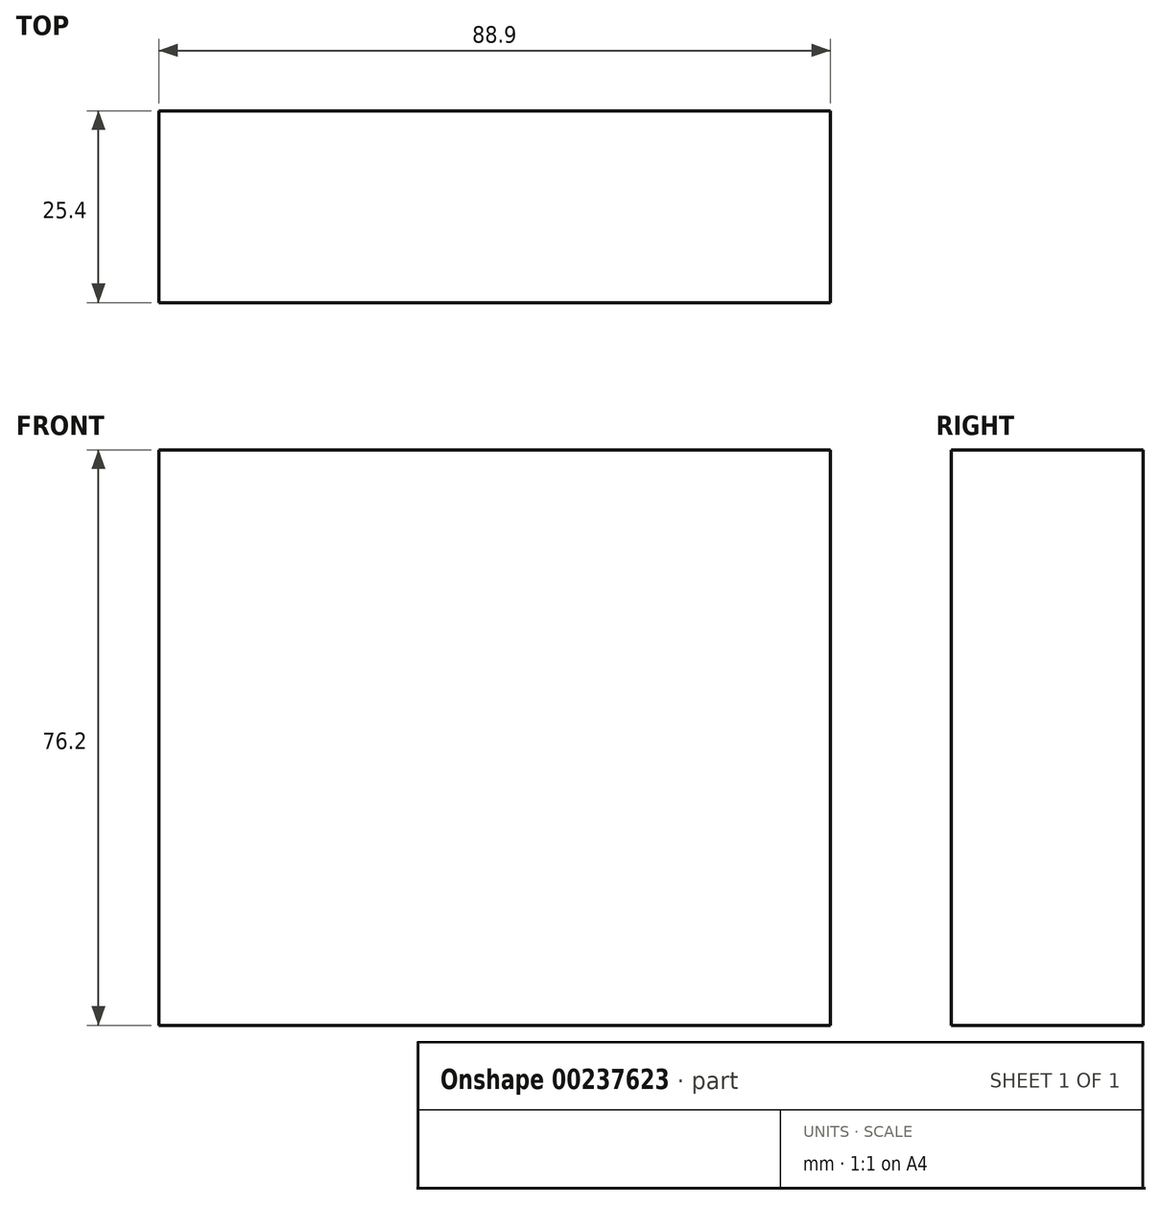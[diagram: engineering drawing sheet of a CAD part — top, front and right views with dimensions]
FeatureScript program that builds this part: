
annotation { "Feature Type Name" : "Feature", "Feature Type Description" : "" }
export const myFeature = defineFeature(function(context is Context, id is Id, definition is map)
    precondition{}
    {
        {
            var Q0;
            Q0=qCreatedBy(makeId("Front.planeOp"),FACE);
            var sketch = newSketch(context, id + "F0", { "sketchPlane" : qUnion([Q0])});
            skLineSegment(sketch, "E0.bottom", {"start": v(20.15, 0) * mm, "end": v(109.05, 0) * mm});
            skLineSegment(sketch, "E0.top", {"start": v(20.15, 76.2) * mm, "end": v(109.05, 76.2) * mm});
            skLineSegment(sketch, "E0.left", {"start": v(20.15, 0) * mm, "end": v(20.15, 76.2) * mm});
            skLineSegment(sketch, "E0.right", {"start": v(109.05, 0) * mm, "end": v(109.05, 76.2) * mm});
            skSolve(sketch);
        }
        {
            var Q0;
            Q0=makeQuery(id+"F0.imprint","IMPRINT",FACE,{"disambiguationData":[TD([[makeQuery(id+"F0.imprint","IMPRINT",EDGE,{"derivedFrom":sQuery(id+"F0.wireOp",EDGE,"E0.bottom")}),1.0]])]});
            extrude(context, id + "F1", {"entities" : qUnion([Q0]), "depth" : 25.4 * mm});
        }
    });
